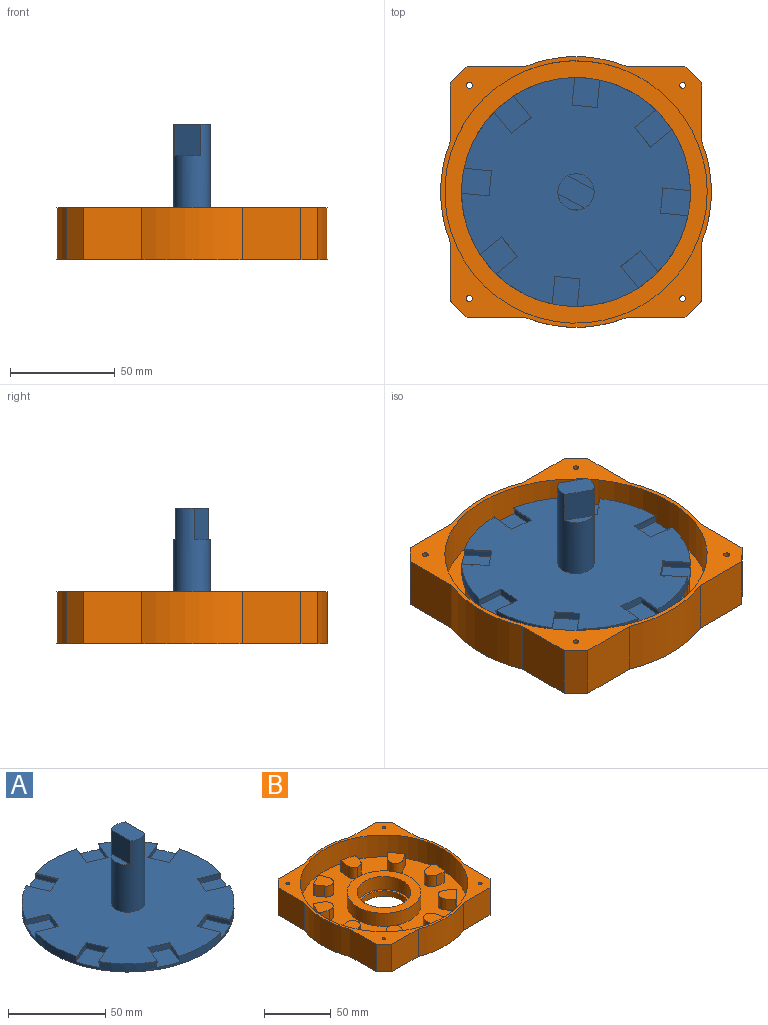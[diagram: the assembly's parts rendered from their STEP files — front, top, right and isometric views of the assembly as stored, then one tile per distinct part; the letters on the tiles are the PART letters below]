
ASSEMBLY  parts=2 mates=1
PART A: 90 faces, bbox 109.2x109.2x50 mm
  f0: plane 17.3x10mm, normal (0,0,1), area 162.8mm2, adj f85,f86,f88
  f1: plane 12.01x4.98mm, normal (-0.38,0.92,0), area 47.2mm2, adj f2,f3,f27,f36,f79,f81,f82,f84
  f2: plane 12.14x5.03mm, normal (-0.92,-0.38,0), area 41.7mm2, adj f1,f25,f36,f84
  f3: plane 12.14x5.03mm, normal (0.92,0.38,0), area 41.7mm2, adj f1,f25,f36,f81
  f4: plane 12.01x4.98mm, normal (0.38,0.92,0), area 47.2mm2, adj f5,f6,f27,f35,f73,f75,f76,f78
  f5: plane 12.14x5.03mm, normal (0.92,-0.38,0), area 41.7mm2, adj f4,f25,f35,f78
  f6: plane 12.14x5.03mm, normal (-0.92,0.38,0), area 41.7mm2, adj f4,f25,f35,f75
  f7: plane 12.01x4.98mm, normal (0.92,0.38,0), area 47.2mm2, adj f8,f9,f27,f34,f67,f69,f70,f72
  f8: plane 12.14x5.03mm, normal (0.38,-0.92,0), area 41.7mm2, adj f7,f25,f34,f72
  f9: plane 12.14x5.03mm, normal (-0.38,0.92,0), area 41.7mm2, adj f7,f25,f34,f69
  f10: plane 12.01x4.98mm, normal (0.92,-0.38,0), area 47.2mm2, adj f11,f12,f27,f33,f61,f63,f64,f66
  f11: plane 12.14x5.03mm, normal (-0.38,-0.92,0), area 41.7mm2, adj f10,f25,f33,f66
  f12: plane 12.14x5.03mm, normal (0.38,0.92,0), area 41.7mm2, adj f10,f25,f33,f63
  f13: plane 12.01x4.98mm, normal (0.38,-0.92,0), area 47.2mm2, adj f14,f15,f27,f32,f55,f57,f58,f60
  f14: plane 12.14x5.03mm, normal (0.92,0.38,0), area 41.7mm2, adj f13,f25,f32,f60
  f15: plane 12.14x5.03mm, normal (-0.92,-0.38,0), area 41.7mm2, adj f13,f25,f32,f57
  f16: plane 12.01x4.98mm, normal (-0.38,-0.92,0), area 47.2mm2, adj f17,f18,f27,f31,f49,f51,f52,f54
  f17: plane 12.14x5.03mm, normal (-0.92,0.38,0), area 41.7mm2, adj f16,f25,f31,f54
  f18: plane 12.14x5.03mm, normal (0.92,-0.38,0), area 41.7mm2, adj f16,f25,f31,f51
  f19: plane 12.01x4.98mm, normal (-0.92,-0.38,0), area 47.2mm2, adj f20,f21,f27,f30,f43,f45,f46,f48
  f20: plane 12.14x5.03mm, normal (0.38,-0.92,0), area 41.7mm2, adj f19,f25,f30,f48
  f21: plane 12.14x5.03mm, normal (-0.38,0.92,0), area 41.7mm2, adj f19,f25,f30,f45
  f22: plane 12.01x4.98mm, normal (-0.92,0.38,0), area 47.2mm2, adj f23,f24,f27,f29,f37,f39,f40,f42
  f23: plane 12.14x5.03mm, normal (0.38,0.92,0), area 41.7mm2, adj f22,f25,f29,f42
  f24: plane 12.14x5.03mm, normal (-0.38,-0.92,0), area 41.7mm2, adj f22,f25,f29,f39
  f25: cylinder r=54.59mm len=109.19mm, axis (0,0,-1), area 1394.6mm2, adj f2,f3,f5,f6,f8,f9,f11,f12
  f26: cylinder r=54.59mm len=0.5mm, axis (0,0,-1), area 0.2mm2, adj f25,f27,f47,f48
  f27: plane 109.19x109.19mm, normal (0,0,1), area 7840.6mm2, adj f1,f4,f7,f10,f13,f16,f19,f22
  f28: plane 109.19x109.19mm, normal (0,0,-1), area 9363.8mm2, adj f25
  f29: plane 17.11x17.04mm, normal (0,0,1), area 174.2mm2, adj f22,f23,f24,f25
  f30: plane 17.11x17.04mm, normal (0,0,1), area 174.2mm2, adj f19,f20,f21,f25
  f31: plane 17.11x17.04mm, normal (0,0,1), area 174.2mm2, adj f16,f17,f18,f25
  f32: plane 17.11x17.04mm, normal (0,0,1), area 174.2mm2, adj f13,f14,f15,f25
  f33: plane 17.11x17.04mm, normal (0,0,1), area 174.2mm2, adj f10,f11,f12,f25
  f34: plane 17.11x17.04mm, normal (0,0,1), area 174.2mm2, adj f7,f8,f9,f25
  f35: plane 17.11x17.04mm, normal (0,0,1), area 174.2mm2, adj f4,f5,f6,f25
  f36: plane 17.11x17.04mm, normal (0,0,1), area 174.2mm2, adj f1,f2,f3,f25
  f37: plane 12.14x5.03mm, normal (-0.38,-0.92,0), area 6.6mm2, adj f22,f27,f38,f39
  f38: plane 0.5x0.05mm, normal (-0.46,-0.89,0), area 0mm2, adj f25,f27,f37,f39
  f39: plane 12.38x5.49mm, normal (0,0,-1), area 6.6mm2, adj f22,f24,f25,f37,f38
  f40: plane 12.14x5.03mm, normal (0.38,0.92,0), area 6.6mm2, adj f22,f27,f41,f42
  f41: plane 0.5x0.05mm, normal (0.33,0.94,0), area 0mm2, adj f25,f27,f40,f42
  f42: plane 12.33x5.51mm, normal (0,0,-1), area 6.6mm2, adj f22,f23,f25,f40,f41
  f43: plane 12.14x5.03mm, normal (-0.38,0.92,0), area 6.6mm2, adj f19,f27,f44,f45
  f44: plane 0.5x0.05mm, normal (-0.45,0.89,0), area 0mm2, adj f25,f27,f43,f45
  f45: plane 12.38x5.49mm, normal (0,0,-1), area 6.6mm2, adj f19,f21,f25,f43,f44
  f46: plane 12.14x5.03mm, normal (0.38,-0.92,0), area 6.6mm2, adj f19,f27,f47,f48
  f47: plane 0.5x0.05mm, normal (0.31,-0.95,0), area 0mm2, adj f26,f27,f46,f48
  f48: plane 12.33x5.51mm, normal (0,0,-1), area 6.6mm2, adj f19,f20,f26,f46,f47
  f49: plane 12.14x5.03mm, normal (0.92,-0.38,0), area 6.6mm2, adj f16,f27,f50,f51
  f50: plane 0.5x0.05mm, normal (0.9,-0.44,0), area 0mm2, adj f25,f27,f49,f51
  f51: plane 12.38x5.49mm, normal (0,0,-1), area 6.6mm2, adj f16,f18,f25,f49,f50
  f52: plane 12.14x5.03mm, normal (-0.92,0.38,0), area 6.6mm2, adj f16,f27,f53,f54
  f53: plane 0.5x0.05mm, normal (-0.95,0.32,0), area 0mm2, adj f25,f27,f52,f54
  f54: plane 12.33x5.51mm, normal (0,0,-1), area 6.6mm2, adj f16,f17,f25,f52,f53
  f55: plane 12.14x5.03mm, normal (-0.92,-0.38,0), area 6.6mm2, adj f13,f27,f56,f57
  f56: plane 0.5x0.05mm, normal (-0.9,-0.44,0), area 0mm2, adj f25,f27,f55,f57
  f57: plane 12.38x5.49mm, normal (0,0,-1), area 6.6mm2, adj f13,f15,f25,f55,f56
  f58: plane 12.14x5.03mm, normal (0.92,0.38,0), area 6.6mm2, adj f13,f27,f59,f60
  f59: plane 0.5x0.05mm, normal (0.95,0.32,0), area 0mm2, adj f25,f27,f58,f60
  f60: plane 12.33x5.51mm, normal (0,0,-1), area 6.6mm2, adj f13,f14,f25,f58,f59
  f61: plane 12.14x5.03mm, normal (0.38,0.92,0), area 6.6mm2, adj f10,f27,f62,f63
  f62: plane 0.5x0.05mm, normal (0.44,0.9,0), area 0mm2, adj f25,f27,f61,f63
  f63: plane 12.38x5.49mm, normal (0,0,-1), area 6.6mm2, adj f10,f12,f25,f61,f62
  f64: plane 12.14x5.03mm, normal (-0.38,-0.92,0), area 6.6mm2, adj f10,f27,f65,f66
  f65: plane 0.5x0.05mm, normal (-0.32,-0.95,0), area 0mm2, adj f25,f27,f64,f66
  f66: plane 12.33x5.51mm, normal (0,0,-1), area 6.6mm2, adj f10,f11,f25,f64,f65
  f67: plane 12.14x5.03mm, normal (-0.38,0.92,0), area 6.6mm2, adj f7,f27,f68,f69
  f68: plane 0.5x0.05mm, normal (-0.31,0.95,0), area 0mm2, adj f25,f27,f67,f69
  f69: plane 12.33x5.51mm, normal (0,0,-1), area 6.6mm2, adj f7,f9,f25,f67,f68
  f70: plane 12.14x5.03mm, normal (0.38,-0.92,0), area 6.6mm2, adj f7,f27,f71,f72
  f71: plane 0.5x0.05mm, normal (0.47,-0.88,0), area 0mm2, adj f25,f27,f70,f72
  f72: plane 12.38x5.49mm, normal (0,0,-1), area 6.6mm2, adj f7,f8,f25,f70,f71
  f73: plane 12.14x5.03mm, normal (-0.92,0.38,0), area 6.6mm2, adj f4,f27,f74,f75
  f74: plane 0.5x0.05mm, normal (-0.9,0.43,0), area 0mm2, adj f25,f27,f73,f75
  f75: plane 12.38x5.49mm, normal (0,0,-1), area 6.6mm2, adj f4,f6,f25,f73,f74
  f76: plane 12.14x5.03mm, normal (0.92,-0.38,0), area 6.6mm2, adj f4,f27,f77,f78
  f77: plane 0.5x0.05mm, normal (0.95,-0.32,0), area 0mm2, adj f25,f27,f76,f78
  f78: plane 12.33x5.51mm, normal (0,0,-1), area 6.6mm2, adj f4,f5,f25,f76,f77
  f79: plane 12.14x5.03mm, normal (0.92,0.38,0), area 6.6mm2, adj f1,f27,f80,f81
  f80: plane 0.5x0.05mm, normal (0.92,0.4,0), area 0mm2, adj f25,f27,f79,f81
  f81: plane 12.38x5.49mm, normal (0,0,-1), area 6.6mm2, adj f1,f3,f25,f79,f80
  f82: plane 12.14x5.03mm, normal (-0.92,-0.38,0), area 6.6mm2, adj f1,f27,f83,f84
  f83: plane 0.5x0.05mm, normal (-0.95,-0.31,0), area 0mm2, adj f25,f27,f82,f84
  f84: plane 12.33x5.51mm, normal (0,0,-1), area 6.6mm2, adj f1,f2,f25,f82,f83
  f85: cylinder r=8.65mm len=44.83mm, axis (0,0,-1), area 1941.1mm2, adj f0,f27,f86,f87,f88,f89
  f86: plane 15x14.12mm, normal (-1,0,0), area 211.8mm2, adj f0,f85,f87
  f87: plane 14.12x3.65mm, normal (0,0,1), area 36.1mm2, adj f85,f86
  f88: plane 15x14.12mm, normal (1,0,0), area 211.8mm2, adj f0,f85,f89
  f89: plane 14.12x3.65mm, normal (0,0,1), area 36.1mm2, adj f85,f88
PART B: 101 faces, bbox 129.2x129.2x25 mm
  f0: plane 125.19x125.19mm, normal (0,0,1), area 8600.7mm2, adj f3,f4,f5,f7,f8,f9,f11,f12
  f1: plane 129.19x129.19mm, normal (0,0,-1), area 13762.8mm2, adj f38,f39,f40,f41,f42,f43,f44,f45
  f2: plane 15.17x14.85mm, normal (0,0,1), area 148.1mm2, adj f3,f4,f5,f74,f75,f92,f93
  f3: plane 10x6.32mm, normal (-0.83,-0.56,0), area 76.1mm2, adj f0,f2,f74,f93
  f4: plane 10x9.97mm, normal (-0.42,0.91,0), area 110mm2, adj f0,f2,f92,f93
  f5: plane 10x6.62mm, normal (0.93,0.36,0), area 70.9mm2, adj f0,f2,f75,f92
  f6: plane 15.44x14.27mm, normal (0,0,1), area 148.1mm2, adj f7,f8,f9,f76,f77,f94,f95
  f7: plane 10x7.32mm, normal (-0.28,-0.96,0), area 76.1mm2, adj f0,f6,f76,f94
  f8: plane 10x9.96mm, normal (-0.91,0.42,0), area 110mm2, adj f0,f6,f94,f95
  f9: plane 10x6.2mm, normal (0.49,0.87,0), area 70.9mm2, adj f0,f6,f77,f95
  f10: plane 14.77x14.07mm, normal (0,0,1), area 148.1mm2, adj f11,f12,f13,f60,f61,f78,f79
  f11: plane 10x6.96mm, normal (0.4,-0.91,0), area 76.1mm2, adj f0,f10,f60,f78
  f12: plane 10.63x10mm, normal (-0.97,-0.26,0), area 110mm2, adj f0,f10,f78,f79
  f13: plane 10x6.97mm, normal (-0.19,0.98,0), area 70.9mm2, adj f0,f10,f61,f79
  f14: plane 15.69x14.86mm, normal (0,0,1), area 148.1mm2, adj f15,f16,f17,f62,f63,f80,f81
  f15: plane 10x6.84mm, normal (0.9,-0.44,0), area 76.1mm2, adj f0,f14,f62,f80
  f16: plane 10x9mm, normal (-0.57,-0.82,0), area 110mm2, adj f0,f14,f80,f81
  f17: plane 10x5.51mm, normal (-0.78,0.63,0), area 70.9mm2, adj f0,f14,f63,f81
  f18: plane 14.14x13.08mm, normal (0,0,1), area 148.1mm2, adj f19,f20,f21,f64,f65,f82,f83
  f19: plane 10x7.39mm, normal (0.97,0.24,0), area 76.1mm2, adj f0,f18,f64,f82
  f20: plane 10.96x10mm, normal (0.09,-1,0), area 110mm2, adj f0,f18,f82,f83
  f21: plane 10x7.09mm, normal (-1,-0.02,0), area 70.9mm2, adj f0,f18,f65,f83
  f22: plane 15.67x15.22mm, normal (0,0,1), area 148.1mm2, adj f23,f24,f25,f66,f67,f84,f85
  f23: plane 10x6.15mm, normal (0.59,0.81,0), area 76.1mm2, adj f0,f22,f66,f84
  f24: plane 10x7.79mm, normal (0.71,-0.71,0), area 110mm2, adj f0,f22,f84,f85
  f25: plane 10x5.36mm, normal (-0.76,-0.66,0), area 70.9mm2, adj f0,f22,f67,f85
  f26: plane 14.2x12.95mm, normal (0,0,1), area 148.1mm2, adj f27,f28,f29,f68,f69,f86,f87
  f27: plane 10x7.6mm, normal (-0.07,1,0), area 76.1mm2, adj f0,f26,f68,f86
  f28: plane 10.95x10mm, normal (1,-0.09,0), area 110mm2, adj f0,f26,f86,f87
  f29: plane 10x7.01mm, normal (-0.16,-0.99,0), area 70.9mm2, adj f0,f26,f69,f87
  f30: plane 15.38x15.32mm, normal (0,0,1), area 148.1mm2, adj f31,f32,f33,f70,f71,f88,f89
  f31: plane 10x5.49mm, normal (-0.69,0.72,0), area 76.1mm2, adj f0,f30,f70,f88
  f32: plane 10x9.02mm, normal (0.82,0.57,0), area 110mm2, adj f0,f30,f88,f89
  f33: plane 10x6.08mm, normal (0.51,-0.86,0), area 70.9mm2, adj f0,f30,f71,f89
  f34: plane 14.94x13.46mm, normal (0,0,1), area 148.1mm2, adj f35,f36,f37,f72,f73,f90,f91
  f35: plane 10x7.57mm, normal (-0.99,0.11,0), area 76.1mm2, adj f0,f34,f72,f90
  f36: plane 10.62x10mm, normal (0.26,0.97,0), area 110mm2, adj f0,f34,f90,f91
  f37: plane 10x6.71mm, normal (0.95,-0.33,0), area 70.9mm2, adj f0,f34,f73,f91
  f38: plane 28.07x25mm, normal (-1,0,0), area 701.8mm2, adj f1,f39,f56,f59
  f39: cylinder r=64.59mm len=47.85mm, axis (0,0,-1), area 1225.6mm2, adj f1,f38,f40,f59
  f40: plane 28.07x25mm, normal (-1,0,0), area 701.8mm2, adj f1,f39,f41,f59
  f41: plane 25x8mm, normal (-0.71,-0.71,0), area 282.8mm2, adj f1,f40,f42,f59
  f42: plane 28.07x25mm, normal (0,-1,0), area 701.8mm2, adj f1,f41,f43,f59
  f43: cylinder r=64.59mm len=47.85mm, axis (0,0,-1), area 1225.6mm2, adj f1,f42,f44,f59
  f44: plane 28.07x25mm, normal (0,-1,0), area 701.8mm2, adj f1,f43,f45,f59
  f45: plane 25x8mm, normal (0.71,-0.71,0), area 282.8mm2, adj f1,f44,f46,f59
  f46: plane 28.07x25mm, normal (1,0,0), area 701.8mm2, adj f1,f45,f47,f59
  f47: cylinder r=64.59mm len=47.85mm, axis (0,0,-1), area 1225.6mm2, adj f1,f46,f48,f59
  f48: plane 28.07x25mm, normal (1,0,0), area 701.8mm2, adj f1,f47,f49,f59
  f49: plane 25x8mm, normal (0.71,0.71,0), area 282.8mm2, adj f1,f48,f50,f59
  f50: plane 28.07x25mm, normal (0,1,0), area 701.8mm2, adj f1,f49,f51,f59
  f51: cylinder r=64.59mm len=47.85mm, axis (0,0,-1), area 1225.6mm2, adj f1,f50,f52,f59
  f52: plane 28.07x25mm, normal (0,1,0), area 701.8mm2, adj f1,f51,f56,f59
  f53: cylinder r=1.4mm len=25mm, axis (0,0,-1), area 219.9mm2, adj f1,f59
  f54: cylinder r=1.4mm len=25mm, axis (0,0,-1), area 219.9mm2, adj f1,f59
  f55: cylinder r=1.4mm len=25mm, axis (0,0,-1), area 219.9mm2, adj f1,f59
  f56: plane 25x8mm, normal (-0.71,0.71,0), area 282.8mm2, adj f1,f38,f52,f59
  f57: cylinder r=62.59mm len=125.19mm, axis (0,0,-1), area 7865.9mm2, adj f0,f59
  f58: cylinder r=1.4mm len=25mm, axis (0,0,-1), area 219.9mm2, adj f1,f59
  f59: plane 129.19x129.19mm, normal (0,0,1), area 2528.9mm2, adj f38,f39,f40,f41,f42,f43,f44,f45
  f60: cylinder r=6mm len=10mm, axis (0,0,1), area 81mm2, adj f0,f10,f11,f61
  f61: cylinder r=6mm len=10mm, axis (0,0,-1), area 88mm2, adj f0,f10,f13,f60
  f62: cylinder r=6mm len=10mm, axis (0,0,1), area 81mm2, adj f0,f14,f15,f63
  f63: cylinder r=6mm len=10mm, axis (0,0,-1), area 88mm2, adj f0,f14,f17,f62
  f64: cylinder r=6mm len=10mm, axis (0,0,1), area 81mm2, adj f0,f18,f19,f65
  f65: cylinder r=6mm len=10mm, axis (0,0,-1), area 88mm2, adj f0,f18,f21,f64
  f66: cylinder r=6mm len=10mm, axis (0,0,1), area 81mm2, adj f0,f22,f23,f67
  f67: cylinder r=6mm len=10mm, axis (0,0,-1), area 88mm2, adj f0,f22,f25,f66
  f68: cylinder r=6mm len=10mm, axis (0,0,1), area 81mm2, adj f0,f26,f27,f69
  f69: cylinder r=6mm len=10mm, axis (0,0,-1), area 88mm2, adj f0,f26,f29,f68
  f70: cylinder r=6mm len=10mm, axis (0,0,1), area 81mm2, adj f0,f30,f31,f71
  f71: cylinder r=6mm len=10mm, axis (0,0,-1), area 88mm2, adj f0,f30,f33,f70
  f72: cylinder r=6mm len=10mm, axis (0,0,1), area 81mm2, adj f0,f34,f35,f73
  f73: cylinder r=6mm len=10mm, axis (0,0,-1), area 88mm2, adj f0,f34,f37,f72
  f74: cylinder r=6mm len=10mm, axis (0,0,1), area 81mm2, adj f0,f2,f3,f75
  f75: cylinder r=6mm len=10mm, axis (0,0,-1), area 88mm2, adj f0,f2,f5,f74
  f76: cylinder r=6mm len=10mm, axis (0,0,1), area 81mm2, adj f0,f6,f7,f77
  f77: cylinder r=6mm len=10mm, axis (0,0,-1), area 88mm2, adj f0,f6,f9,f76
  f78: cylinder r=1mm len=10mm, axis (0,0,-1), area 17.3mm2, adj f0,f10,f11,f12
  f79: cylinder r=1mm len=10mm, axis (0,0,1), area 16.4mm2, adj f0,f10,f12,f13
  f80: cylinder r=1mm len=10mm, axis (0,0,-1), area 17.3mm2, adj f0,f14,f15,f16
  f81: cylinder r=1mm len=10mm, axis (0,0,1), area 16.4mm2, adj f0,f14,f16,f17
  f82: cylinder r=1mm len=10mm, axis (0,0,-1), area 17.3mm2, adj f0,f18,f19,f20
  f83: cylinder r=1mm len=10mm, axis (0,0,1), area 16.4mm2, adj f0,f18,f20,f21
  f84: cylinder r=1mm len=10mm, axis (0,0,-1), area 17.3mm2, adj f0,f22,f23,f24
  f85: cylinder r=1mm len=10mm, axis (0,0,1), area 16.4mm2, adj f0,f22,f24,f25
  f86: cylinder r=1mm len=10mm, axis (0,0,-1), area 17.3mm2, adj f0,f26,f27,f28
  f87: cylinder r=1mm len=10mm, axis (0,0,1), area 16.4mm2, adj f0,f26,f28,f29
  f88: cylinder r=1mm len=10mm, axis (0,0,-1), area 17.3mm2, adj f0,f30,f31,f32
  f89: cylinder r=1mm len=10mm, axis (0,0,1), area 16.4mm2, adj f0,f30,f32,f33
  f90: cylinder r=1mm len=10mm, axis (0,0,-1), area 17.3mm2, adj f0,f34,f35,f36
  f91: cylinder r=1mm len=10mm, axis (0,0,1), area 16.4mm2, adj f0,f34,f36,f37
  f92: cylinder r=1mm len=10mm, axis (0,0,1), area 16.4mm2, adj f0,f2,f4,f5
  f93: cylinder r=1mm len=10mm, axis (0,0,-1), area 17.3mm2, adj f0,f2,f3,f4
  f94: cylinder r=1mm len=10mm, axis (0,0,-1), area 17.3mm2, adj f0,f6,f7,f8
  f95: cylinder r=1mm len=10mm, axis (0,0,1), area 16.4mm2, adj f0,f6,f8,f9
  f96: cylinder r=20.15mm len=40.3mm, axis (0,0,-1), area 1519.3mm2, adj f98,f100
  f97: cylinder r=27.5mm len=55mm, axis (0,0,-1), area 2073.5mm2, adj f0,f98
  f98: plane 55x55mm, normal (0,0,1), area 1100.3mm2, adj f96,f97
  f99: cylinder r=18.5mm len=37mm, axis (0,0,-1), area 581.2mm2, adj f1,f100
  f100: plane 40.3x40.3mm, normal (0,0,1), area 200.3mm2, adj f96,f99
PLACE A rot(axis=(0,0,-1),118.2deg) t=(-40.33,-52.07,-2.65)mm
PLACE B t=(-40.33,-52.07,-17.48)mm fixed
MATE revolute B.f57 <-> A.f85  axis (0,0,1) through (-40.33,-52.07,-12.48)mm
